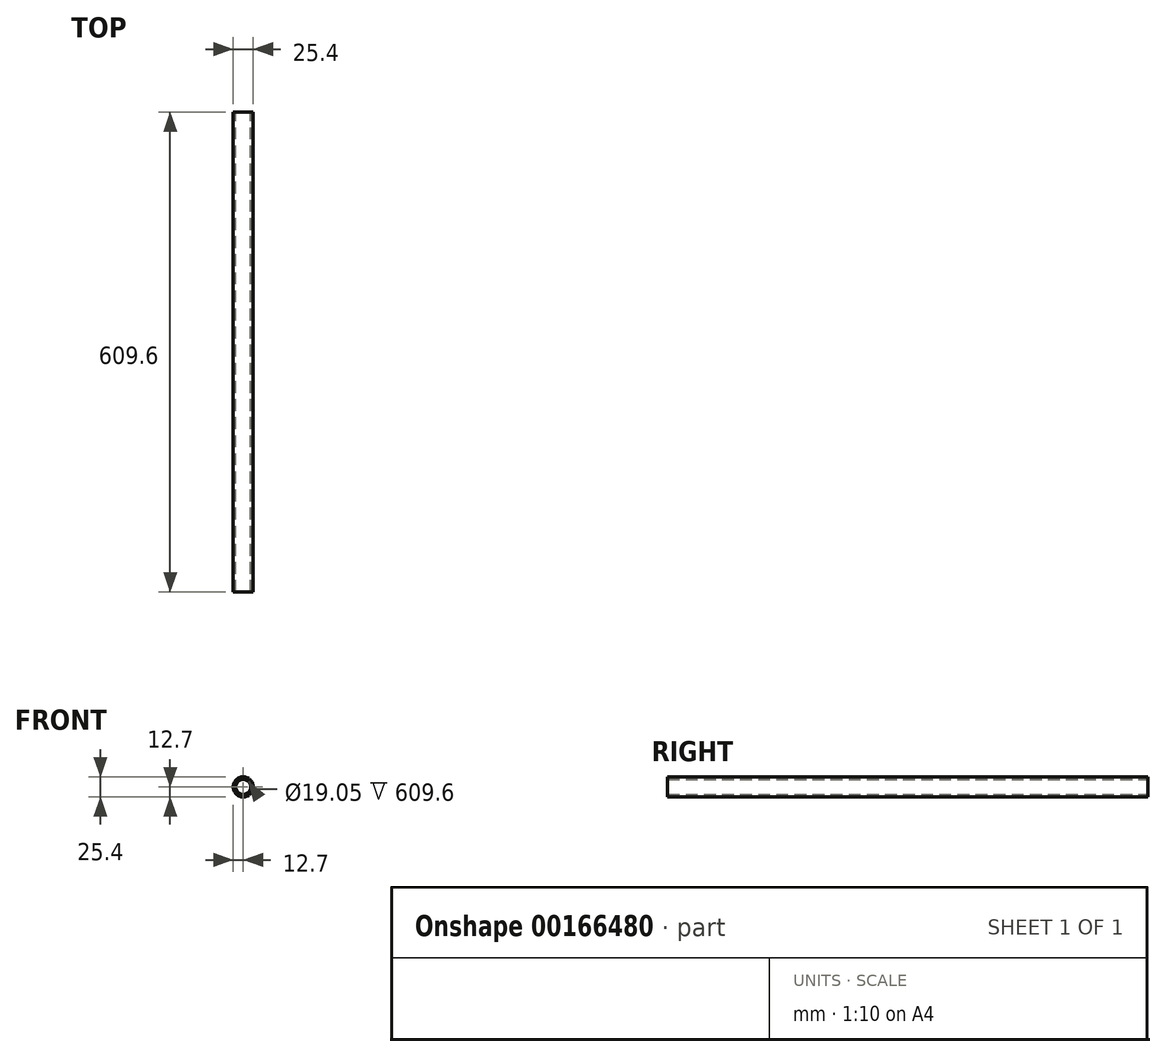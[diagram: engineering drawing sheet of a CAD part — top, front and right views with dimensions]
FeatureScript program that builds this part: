
annotation { "Feature Type Name" : "Feature", "Feature Type Description" : "" }
export const myFeature = defineFeature(function(context is Context, id is Id, definition is map)
    precondition{}
    {
        {
            var Q0;
            Q0=qCreatedBy(makeId("Front.planeOp"),FACE);
            var sketch = newSketch(context, id + "F0", { "sketchPlane" : qUnion([Q0])});
            skCircle(sketch, "E0", {"center": v(0, 0) * mm, "radius": 12.7 * mm});
            skSolve(sketch);
        }
        {
            var Q0;
            Q0 = qSketchRegion(id + "F0", true);
            extrude(context, id + "F1", {"entities" : qUnion([Q0]), "depth" : 609.6 * mm});
        }
        {
            var Q0;
            Q0=qCreatedBy(makeId("Front.planeOp"),FACE);
            var sketch = newSketch(context, id + "F2", { "sketchPlane" : qUnion([Q0])});
            skCircle(sketch, "E1", {"center": v(0, 0) * mm, "radius": 9.53 * mm});
            skSolve(sketch);
        }
        {
            var Q0;
            Q0 = qSketchRegion(id + "F2", true);
            extrude(context, id + "F3", {"entities" : qUnion([Q0]), "operationType" : NewBodyOperationType.REMOVE, "depth" : 609.6 * mm});
        }
    });
